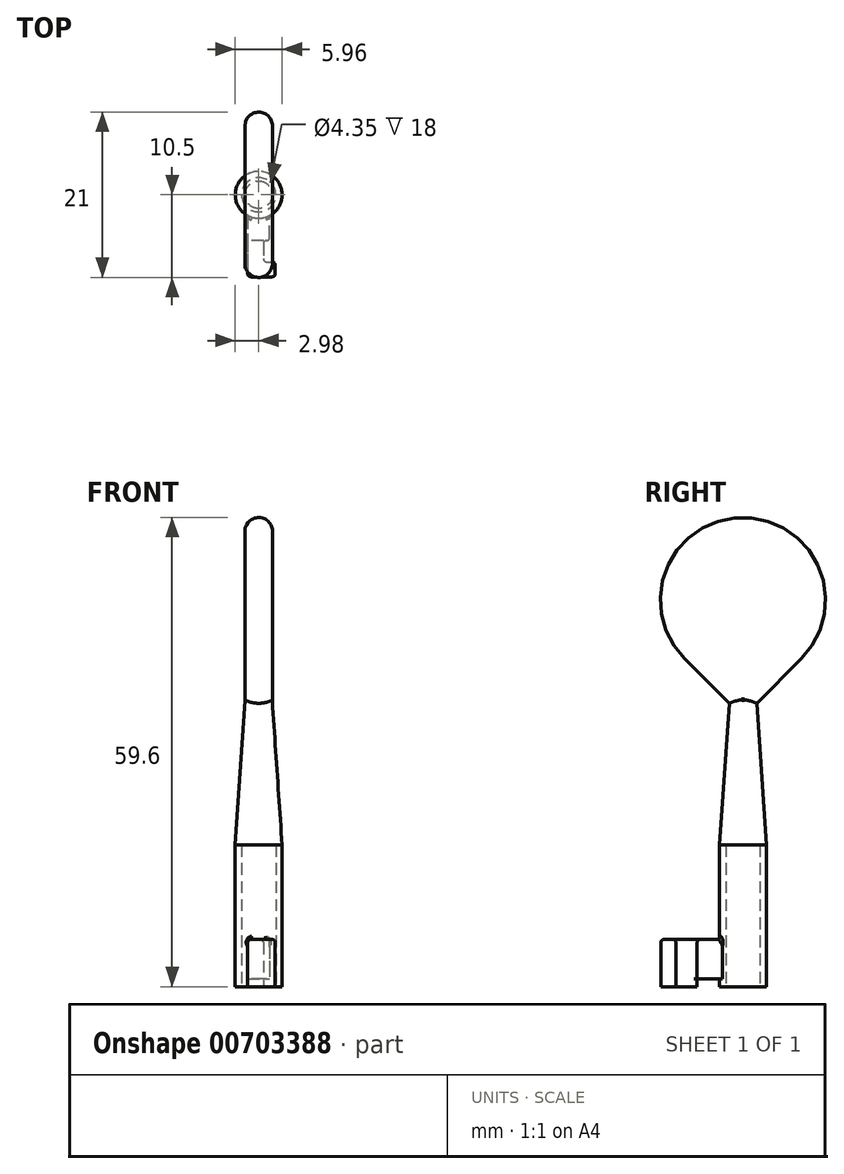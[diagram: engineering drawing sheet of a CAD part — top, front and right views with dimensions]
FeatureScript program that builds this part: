
annotation { "Feature Type Name" : "Feature", "Feature Type Description" : "" }
export const myFeature = defineFeature(function(context is Context, id is Id, definition is map)
    precondition{}
    {
        {
            var Q0;
            Q0=qCreatedBy(makeId("Top.planeOp"),FACE);
            var sketch = newSketch(context, id + "F0", { "sketchPlane" : qUnion([Q0])});
            skCircle(sketch, "E0", {"center": v(0, 0) * mm, "radius": 2.17 * mm});
            skCircle(sketch, "E1", {"center": v(0, 0) * mm, "radius": 2.98 * mm});
            skLineSegment(sketch, "E2", {"start": v(-1.4, -2.63) * mm, "end": v(-1.4, -10.43) * mm});
            skLineSegment(sketch, "E3", {"start": v(1.4, -5.83) * mm, "end": v(0.6, -5.83) * mm});
            skLineSegment(sketch, "E4", {"start": v(0.6, -5.83) * mm, "end": v(0.6, -8.53) * mm});
            skLineSegment(sketch, "E5", {"start": v(0.6, -8.53) * mm, "end": v(2.1, -8.53) * mm});
            skLineSegment(sketch, "E6", {"start": v(2.1, -8.53) * mm, "end": v(2.1, -10.43) * mm});
            skLineSegment(sketch, "E7.trimOffspring", {"start": v(1.4, -5.83) * mm, "end": v(1.4, -2.63) * mm});
            skLineSegment(sketch, "E8", {"start": v(-1.4, -10.43) * mm, "end": v(2.1, -10.43) * mm});
            skLineSegment(sketch, "E9", {"start": v(0.6, -5.83) * mm, "end": v(-1.4, -5.83) * mm});
            skSolve(sketch);
        }
        {
            var Q0;
            {var subQ0=sQuery(id+"F0.wireOp",EDGE,"E2");Q0=makeQuery(id+"F0.imprint","IMPRINT",FACE,{"disambiguationData":[TD([[makeQuery(id+"F0.imprint","IMPRINT",EDGE,{"derivedFrom":subQ0}),1.0]])]});}
            var Q1;
            Q1=makeQuery(id+"F0.imprint","IMPRINT",FACE,{"disambiguationData":[TD([[makeQuery(id+"F0.imprint","IMPRINT",EDGE,{"derivedFrom":sQuery(id+"F0.wireOp",EDGE,"E4")}),-1.0]])]});
            extrude(context, id + "F1", {"entities" : qUnion([Q0, Q1]), "depth" : 6 * mm, "offsetDistance" : 25 * mm});
        }
        {
            var Q0;
            Q0=makeQuery(id+"F0.imprint","IMPRINT",FACE,{"disambiguationData":[TD([[makeQuery(id+"F0.imprint","IMPRINT",EDGE,{"derivedFrom":sQuery(id+"F0.wireOp",EDGE,"E3")}),-1.0]])]});
            extrude(context, id + "F2", {"entities" : qUnion([Q0]), "operationType" : NewBodyOperationType.REMOVE, "depth" : 1 * mm, "offsetDistance" : 25 * mm});
        }
        {
            var Q0;
            Q0=makeQuery(id+"F0.imprint","IMPRINT",FACE,{"disambiguationData":[TD([[makeQuery(id+"F0.imprint","IMPRINT",EDGE,{"derivedFrom":sQuery(id+"F0.wireOp",EDGE,"E0")}),-1.0]])]});
            extrude(context, id + "F3", {"entities" : qUnion([Q0]), "operationType" : NewBodyOperationType.ADD, "depth" : 18 * mm, "offsetDistance" : 25 * mm});
        }
        {
            var Q0;
            Q0=qCreatedBy(makeId("Top.planeOp"),FACE);
            cPlane(context, id + "F4", {"entities" : qUnion([Q0]), "cplaneType" : CPlaneType.OFFSET, "offset" : 18 * mm, "width" : 150 * mm, "height" : 150 * mm});
        }
        {
            var Q0;
            Q0=qCreatedBy(id+"F4.planeOp",FACE);
            var sketch = newSketch(context, id + "F5", { "sketchPlane" : qUnion([Q0])});
            skCircle(sketch, "E10", {"center": v(0, 0) * mm, "radius": 2.98 * mm});
            skSolve(sketch);
        }
        {
            var Q0;
            Q0=qCreatedBy(makeId("Top.planeOp"),FACE);
            cPlane(context, id + "F6", {"entities" : qUnion([Q0]), "cplaneType" : CPlaneType.OFFSET, "offset" : 36 * mm, "width" : 150 * mm, "height" : 150 * mm});
        }
        {
            var Q0;
            Q0=qCreatedBy(id+"F6.planeOp",FACE);
            var sketch = newSketch(context, id + "F7", { "sketchPlane" : qUnion([Q0])});
            skCircle(sketch, "E11", {"center": v(0, 0) * mm, "radius": 1.75 * mm});
            skSolve(sketch);
        }
        {
            var Q1;
            Q1=makeQuery(id+"F7.imprint","IMPRINT",FACE,{"disambiguationData":[TD([[makeQuery(id+"F7.imprint","IMPRINT",EDGE,{"derivedFrom":sQuery(id+"F7.wireOp",EDGE,"E11")}),1.0]])]});
            var Q2;
            Q2=makeQuery(id+"F5.imprint","IMPRINT",FACE,{"disambiguationData":[TD([[makeQuery(id+"F5.imprint","IMPRINT",EDGE,{"derivedFrom":sQuery(id+"F5.wireOp",EDGE,"E10")}),1.0]])]});
            loft(context, id + "F8", {"operationType" : NewBodyOperationType.ADD, "sheetProfilesArray" : [{ "sheetProfileEntities" : qUnion([Q1]) }, { "sheetProfileEntities" : qUnion([Q2]) }]});
        }
        {
            var Q0;
            Q0=qCreatedBy(makeId("Right.planeOp"),FACE);
            var sketch = newSketch(context, id + "F9", { "sketchPlane" : qUnion([Q0])});
            skLineSegment(sketch, "E12", {"start": v(-1.75, 36) * mm, "end": v(1.75, 36) * mm, "construction": true});
            skLineSegment(sketch, "E13", {"start": v(-7.42, 41.67) * mm, "end": v(0, 34.25) * mm});
            skLineSegment(sketch, "E14", {"start": v(0, 34.25) * mm, "end": v(7.42, 41.67) * mm});
            skArc(sketch, "E15", {"start": v(-7.42, 41.67) * mm, "mid": v(0, 59.6) * mm, "end": v(7.42, 41.67) * mm});
            skSolve(sketch);
        }
        {
            var Q0;
            Q0=makeQuery(id+"F9.imprint","IMPRINT",FACE,{"disambiguationData":[TD([[makeQuery(id+"F9.imprint","IMPRINT",EDGE,{"derivedFrom":sQuery(id+"F9.wireOp",EDGE,"E13")}),1.0]])]});
            extrude(context, id + "F10", {"entities" : qUnion([Q0]), "operationType" : NewBodyOperationType.ADD, "endBound" : BoundingType.SYMMETRIC, "depth" : 3.5 * mm, "offsetDistance" : 25 * mm});
        }
        {
            var Q0;
            Q0=makeQuery(id+"F10.opExtrude","CAP_FACE",FACE,{"disambiguationData":[OSD([sQuery(id+"F9.wireOp",EDGE,"E13"),sQuery(id+"F9.wireOp",EDGE,"E14"),sQuery(id+"F9.wireOp",EDGE,"E15"),sQuery(id+"F9.wireOp",EDGE,"61495a9c-b7a5-4a28-98a7-50debadfcde5.0"),sQuery(id+"F9.wireOp",EDGE,"61495a9c-b7a5-4a28-98a7-50debadfcde5.1"),sQuery(id+"F9.wireOp",EDGE,"61495a9c-b7a5-4a28-98a7-50debadfcde5.2")])],"isStart":false});
            var Q1;
            Q1=makeQuery(id+"F10.opExtrude","CAP_FACE",FACE,{"disambiguationData":[OSD([sQuery(id+"F9.wireOp",EDGE,"E13"),sQuery(id+"F9.wireOp",EDGE,"E14"),sQuery(id+"F9.wireOp",EDGE,"E15"),sQuery(id+"F9.wireOp",EDGE,"61495a9c-b7a5-4a28-98a7-50debadfcde5.0"),sQuery(id+"F9.wireOp",EDGE,"61495a9c-b7a5-4a28-98a7-50debadfcde5.1"),sQuery(id+"F9.wireOp",EDGE,"61495a9c-b7a5-4a28-98a7-50debadfcde5.2")])],"isStart":true});
            fillet(context, id + "F11", {"entities" : qUnion([Q0, Q1]), "radius" : 1.75 * mm, "allowEdgeOverflow" : false});
        }
        {
            var Q0;
            Q0=makeQuery(id+"F1.opExtrude","SWEPT_EDGE",EDGE,{"disambiguationData":[OSD([sQuery(id+"F0.wireOp",EDGE,"E2"),sQuery(id+"F0.wireOp",EDGE,"E8")])]});
            var Q1;
            Q1=makeQuery(id+"F1.opExtrude","SWEPT_EDGE",EDGE,{"disambiguationData":[OSD([sQuery(id+"F0.wireOp",EDGE,"E6"),sQuery(id+"F0.wireOp",EDGE,"E8")])]});
            var Q2;
            Q2=makeQuery(id+"F1.opExtrude","SWEPT_EDGE",EDGE,{"disambiguationData":[OSD([sQuery(id+"F0.wireOp",EDGE,"E5"),sQuery(id+"F0.wireOp",EDGE,"E6")])]});
            var Q3;
            Q3=makeQuery(id+"F1.opExtrude","SWEPT_EDGE",EDGE,{"disambiguationData":[OSD([sQuery(id+"F0.wireOp",EDGE,"E4"),sQuery(id+"F0.wireOp",EDGE,"E5")])]});
            var Q4;
            Q4=makeQuery(id+"F1.opExtrude","SWEPT_EDGE",EDGE,{"disambiguationData":[OSD([sQuery(id+"F0.wireOp",EDGE,"E3"),sQuery(id+"F0.wireOp",EDGE,"E7.trimOffspring")])]});
            var Q5;
            Q5=makeQuery(id+"F1.opExtrude","SWEPT_EDGE",EDGE,{"disambiguationData":[OSD([sQuery(id+"F0.wireOp",EDGE,"E1"),sQuery(id+"F0.wireOp",EDGE,"E7.trimOffspring")])]});
            var Q6;
            Q6=makeQuery(id+"F1.opExtrude","SWEPT_EDGE",EDGE,{"disambiguationData":[OSD([sQuery(id+"F0.wireOp",EDGE,"E1"),sQuery(id+"F0.wireOp",EDGE,"E2")])]});
            var Q7;
            Q7=makeQuery(id+"F2.boolean.opBoolean","COPY",EDGE,{"derivedFrom":makeQuery(id+"F2.opExtrude","SWEPT_EDGE",EDGE,{"disambiguationData":[OSD([sQuery(id+"F0.wireOp",EDGE,"E2"),sQuery(id+"F0.wireOp",EDGE,"E9")])]})});
            var Q8;
            Q8=makeQuery(id+"F1.opExtrude","CAP_FACE",FACE,{"disambiguationData":[OSD([sQuery(id+"F0.wireOp",EDGE,"E1"),sQuery(id+"F0.wireOp",EDGE,"E2"),sQuery(id+"F0.wireOp",EDGE,"E3"),sQuery(id+"F0.wireOp",EDGE,"E4"),sQuery(id+"F0.wireOp",EDGE,"E5"),sQuery(id+"F0.wireOp",EDGE,"E6"),sQuery(id+"F0.wireOp",EDGE,"E7.trimOffspring"),sQuery(id+"F0.wireOp",EDGE,"E8")])],"isStart":false});
            var Q9;
            {var subQ0=sQuery(id+"F0.wireOp",EDGE,"E3");var subQ1=sQuery(id+"F0.wireOp",EDGE,"E4");Q9=makeQuery(id+"F2.boolean.opBoolean","SPLIT",EDGE,{"disambiguationData":[topologyDisambiguationEdgeConnected([makeQuery(id+"F1.opExtrude","SWEPT_FACE",FACE,{"disambiguationData":[OSD([subQ0])]})])],"derivedFrom":makeQuery(id+"F1.opExtrude","SWEPT_EDGE",EDGE,{"disambiguationData":[OSD([subQ0,subQ1,sQuery(id+"F0.wireOp",EDGE,"E9")])]})});}
            fillet(context, id + "F12", {"entities" : qUnion([Q0, Q1, Q2, Q3, Q4, Q5, Q6, Q7, Q8, Q9]), "radius" : .4 * mm, "tangentPropagation" : true, "allowEdgeOverflow" : false});
        }
    });
